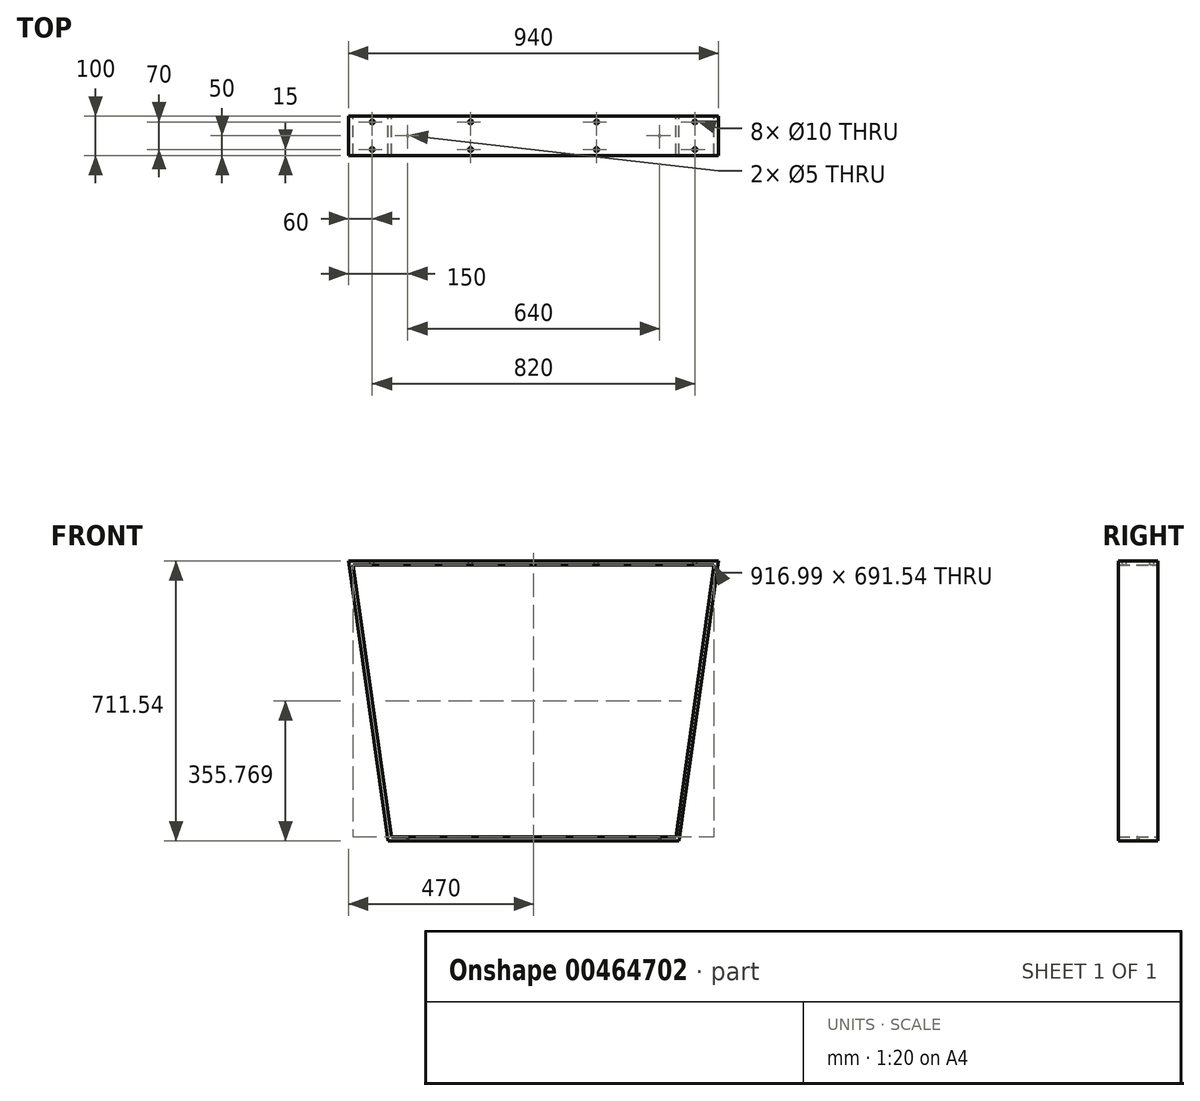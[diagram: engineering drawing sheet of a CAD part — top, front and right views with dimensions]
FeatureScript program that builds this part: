
annotation { "Feature Type Name" : "Feature", "Feature Type Description" : "" }
export const myFeature = defineFeature(function(context is Context, id is Id, definition is map)
    precondition{}
    {
        {
            var Q0;
            Q0=qCreatedBy(makeId("Front.planeOp"),FACE);
            var sketch = newSketch(context, id + "F0", { "sketchPlane" : qUnion([Q0])});
            skLineSegment(sketch, "E0.bottom", {"start": v(470, 375) * mm, "end": v(-470, 375) * mm, "construction": true});
            skLineSegment(sketch, "E0.top", {"start": v(470, -375) * mm, "end": v(-470, -375) * mm, "construction": true});
            skLineSegment(sketch, "E0.left", {"start": v(470, 375) * mm, "end": v(470, -375) * mm, "construction": true});
            skLineSegment(sketch, "E0.right", {"start": v(-470, 375) * mm, "end": v(-470, -375) * mm, "construction": true});
            skPoint(sketch, "E0.middle", {"position": v(0, 0) * mm});
            skLineSegment(sketch, "E1", {"start": v(-470, 336.54) * mm, "end": v(-370, -375) * mm});
            skLineSegment(sketch, "E2", {"start": v(-370, -375) * mm, "end": v(370, -375) * mm});
            skLineSegment(sketch, "E3", {"start": v(370, -375) * mm, "end": v(470, 336.54) * mm});
            skLineSegment(sketch, "E4", {"start": v(470, 336.54) * mm, "end": v(-470, 336.54) * mm});
            skLineSegment(sketch, "E5.0", {"start": v(458.5, 326.54) * mm, "end": v(-458.5, 326.54) * mm});
            skLineSegment(sketch, "E5.1", {"start": v(361.3, -365) * mm, "end": v(458.5, 326.54) * mm});
            skLineSegment(sketch, "E5.2", {"start": v(-361.3, -365) * mm, "end": v(361.3, -365) * mm});
            skLineSegment(sketch, "E5.3", {"start": v(-458.5, 326.54) * mm, "end": v(-361.3, -365) * mm});
            skSolve(sketch);
        }
        {
            var Q0;
            Q0 = qSketchRegion(id + "F0", true);
            extrude(context, id + "F1", {"entities" : qUnion([Q0]), "depth" : 100 * mm, "offsetDistance" : 25 * mm});
        }
        {
            var Q0;
            Q0=makeQuery(id+"F1.opExtrude","SWEPT_FACE",FACE,{"disambiguationData":[OSD([sQuery(id+"F0.wireOp",EDGE,"E2")])]});
            var sketch = newSketch(context, id + "F2", { "sketchPlane" : qUnion([Q0])});
            skPoint(sketch, "E6", {"position": v(-320, 50) * mm});
            skPoint(sketch, "E7", {"position": v(320, 50) * mm});
            skLineSegment(sketch, "E8", {"start": v(-320, 50) * mm, "end": v(-320, 100) * mm});
            skLineSegment(sketch, "E9", {"start": v(-320, 50) * mm, "end": v(-320, 0) * mm});
            skSolve(sketch);
        }
        {
            var Q0;
            Q0=sQuery(id+"F2.wireOp",VERTEX,"E6");
            var Q1;
            Q1=sQuery(id+"F2.wireOp",VERTEX,"E7");
            var Q2;
            Q2=makeQuery(id+"F1.opExtrude","SWEPT_BODY",BODY,{"disambiguationData":[OSD([sQuery(id+"F0.wireOp",EDGE,"E1"),sQuery(id+"F0.wireOp",EDGE,"E3"),sQuery(id+"F0.wireOp",EDGE,"E4"),sQuery(id+"F0.wireOp",EDGE,"E2"),sQuery(id+"F0.wireOp",EDGE,"E5.0"),sQuery(id+"F0.wireOp",EDGE,"E5.1"),sQuery(id+"F0.wireOp",EDGE,"E5.2"),sQuery(id+"F0.wireOp",EDGE,"E5.3")])]});
            hole(context, id + "F3", {"style" : HoleStyle.SIMPLE, "endStyle" : HoleEndStyle.BLIND, "standardTappedOrClearance" : lookupTablePath({ "standard" : "ISO", "engagement" : "75%", "pitch" : "1 mm", "size" : "M6", "type" : "Tapped" }), "standardBlindInLast" : lookupTablePath({ "standard" : "ISO", "engagement" : "75%", "pitch" : "1 mm", "size" : "M6", "type" : "Tapped" }), "holeDiameter" : 5 * mm, "majorDiameter" : 6 * mm, "showTappedDepth" : true, "holeDepth" : 15 * mm, "isTappedThrough" : true, "tappedDepth" : 12 * mm, "tapClearance" : 3, "locations" : qUnion([Q0, Q1]), "scope" : qUnion([Q2])});
        }
        {
            var Q0;
            Q0=makeQuery(id+"F1.opExtrude","SWEPT_FACE",FACE,{"disambiguationData":[OSD([sQuery(id+"F0.wireOp",EDGE,"E4")])]});
            var sketch = newSketch(context, id + "F4", { "sketchPlane" : qUnion([Q0])});
            skLineSegment(sketch, "E10", {"start": v(-470, -50) * mm, "end": v(470, -50) * mm});
            skLineSegment(sketch, "E11.bottom", {"start": v(-410, -15) * mm, "end": v(410, -15) * mm});
            skLineSegment(sketch, "E11.top", {"start": v(-410, -85) * mm, "end": v(410, -85) * mm});
            skLineSegment(sketch, "E11.left", {"start": v(-410, -15) * mm, "end": v(-410, -85) * mm});
            skLineSegment(sketch, "E11.right", {"start": v(410, -15) * mm, "end": v(410, -85) * mm});
            skLineSegment(sketch, "E12", {"start": v(0, 0) * mm, "end": v(0, -100) * mm});
            skLineSegment(sketch, "E13.bottom", {"start": v(-160, -15) * mm, "end": v(160, -15) * mm});
            skLineSegment(sketch, "E13.top", {"start": v(-160, -85) * mm, "end": v(160, -85) * mm});
            skLineSegment(sketch, "E13.left", {"start": v(-160, -15) * mm, "end": v(-160, -85) * mm});
            skLineSegment(sketch, "E13.right", {"start": v(160, -15) * mm, "end": v(160, -85) * mm});
            skLineSegment(sketch, "E14", {"start": v(-154.92, -15) * mm, "end": v(-154.92, -50) * mm});
            skLineSegment(sketch, "E15", {"start": v(-154.92, -50) * mm, "end": v(-154.92, -85) * mm});
            skSolve(sketch);
        }
        {
            var Q0;
            Q0=sQuery(id+"F4.wireOp",VERTEX,"E11.bottom.start");
            var Q1;
            Q1=sQuery(id+"F4.wireOp",VERTEX,"E11.top.start");
            var Q2;
            Q2=sQuery(id+"F4.wireOp",VERTEX,"E13.bottom.start");
            var Q3;
            Q3=sQuery(id+"F4.wireOp",VERTEX,"E13.top.start");
            var Q4;
            Q4=sQuery(id+"F4.wireOp",VERTEX,"E13.top.end");
            var Q5;
            Q5=sQuery(id+"F4.wireOp",VERTEX,"E13.bottom.end");
            var Q6;
            Q6=sQuery(id+"F4.wireOp",VERTEX,"E11.bottom.end");
            var Q7;
            Q7=sQuery(id+"F4.wireOp",VERTEX,"E11.top.end");
            var Q8;
            Q8=makeQuery(id+"F1.opExtrude","SWEPT_BODY",BODY,{"disambiguationData":[OSD([sQuery(id+"F0.wireOp",EDGE,"E1"),sQuery(id+"F0.wireOp",EDGE,"E3"),sQuery(id+"F0.wireOp",EDGE,"E4"),sQuery(id+"F0.wireOp",EDGE,"E2"),sQuery(id+"F0.wireOp",EDGE,"E5.0"),sQuery(id+"F0.wireOp",EDGE,"E5.1"),sQuery(id+"F0.wireOp",EDGE,"E5.2"),sQuery(id+"F0.wireOp",EDGE,"E5.3")])]});
            hole(context, id + "F5", {"style" : HoleStyle.SIMPLE, "endStyle" : HoleEndStyle.BLIND, "standardTappedOrClearance" : lookupTablePath({ "standard" : "ISO", "size" : "10", "type" : "Drilled" }), "standardBlindInLast" : lookupTablePath({ "standard" : "ISO", "size" : "10", "type" : "Drilled" }), "holeDiameter" : 10 * mm, "majorDiameter" : 6 * mm, "holeDepth" : 15 * mm, "isTappedThrough" : true, "tappedDepth" : 12 * mm, "tapClearance" : 3, "locations" : qUnion([Q0, Q1, Q2, Q3, Q4, Q5, Q6, Q7]), "scope" : qUnion([Q8])});
        }
    });
